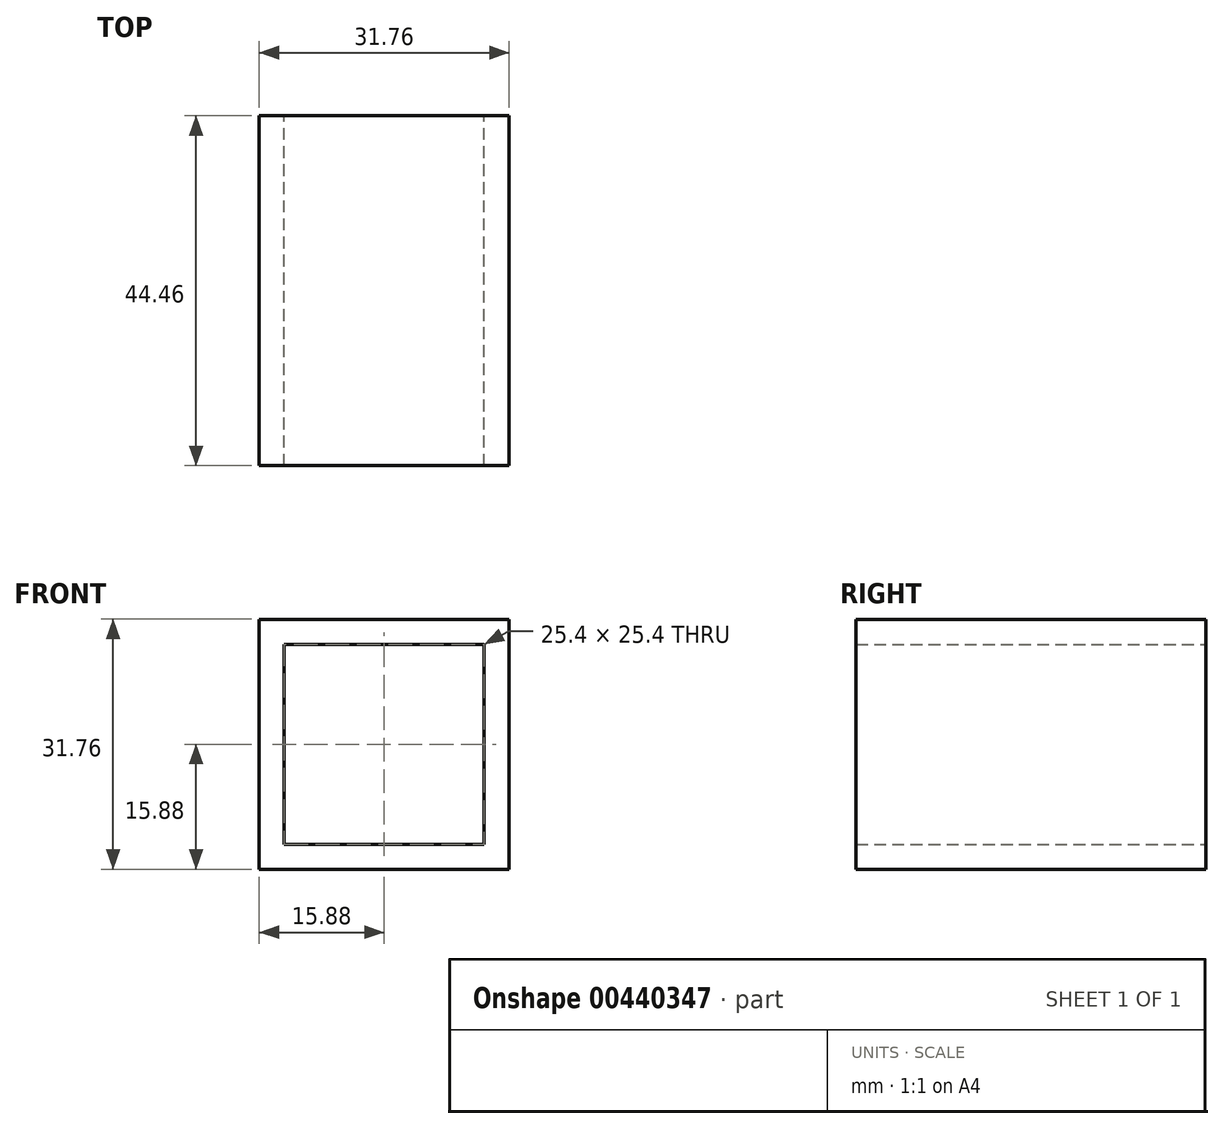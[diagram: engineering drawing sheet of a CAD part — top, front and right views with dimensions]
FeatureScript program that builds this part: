
annotation { "Feature Type Name" : "Feature", "Feature Type Description" : "" }
export const myFeature = defineFeature(function(context is Context, id is Id, definition is map)
    precondition{}
    {
        {
            var Q0;
            Q0=qCreatedBy(makeId("Front.planeOp"),FACE);
            var sketch = newSketch(context, id + "F0", { "sketchPlane" : qUnion([Q0])});
            skLineSegment(sketch, "E0.bottom", {"start": v(-15.87, 15.88) * mm, "end": v(15.88, 15.88) * mm});
            skLineSegment(sketch, "E0.top", {"start": v(-15.88, -15.88) * mm, "end": v(15.88, -15.88) * mm});
            skLineSegment(sketch, "E0.left", {"start": v(-15.87, 15.88) * mm, "end": v(-15.88, -15.88) * mm});
            skLineSegment(sketch, "E0.right", {"start": v(15.88, 15.88) * mm, "end": v(15.88, -15.88) * mm});
            skPoint(sketch, "E0.middle", {"position": v(0, 0) * mm});
            skLineSegment(sketch, "E1.bottom", {"start": v(-12.7, 12.7) * mm, "end": v(12.7, 12.7) * mm});
            skLineSegment(sketch, "E1.top", {"start": v(-12.7, -12.7) * mm, "end": v(12.7, -12.7) * mm});
            skLineSegment(sketch, "E1.left", {"start": v(-12.7, 12.7) * mm, "end": v(-12.7, -12.7) * mm});
            skLineSegment(sketch, "E1.right", {"start": v(12.7, 12.7) * mm, "end": v(12.7, -12.7) * mm});
            skSolve(sketch);
        }
        {
            var Q0;
            Q0=makeQuery(id+"F0.imprint","IMPRINT",FACE,{"disambiguationData":[TD([[makeQuery(id+"F0.imprint","IMPRINT",EDGE,{"derivedFrom":sQuery(id+"F0.wireOp",EDGE,"E0.bottom")}),-1.0]])]});
            extrude(context, id + "F1", {"entities" : qUnion([Q0]), "endBound" : BoundingType.SYMMETRIC, "depth" : 44.45 * mm});
        }
    });
